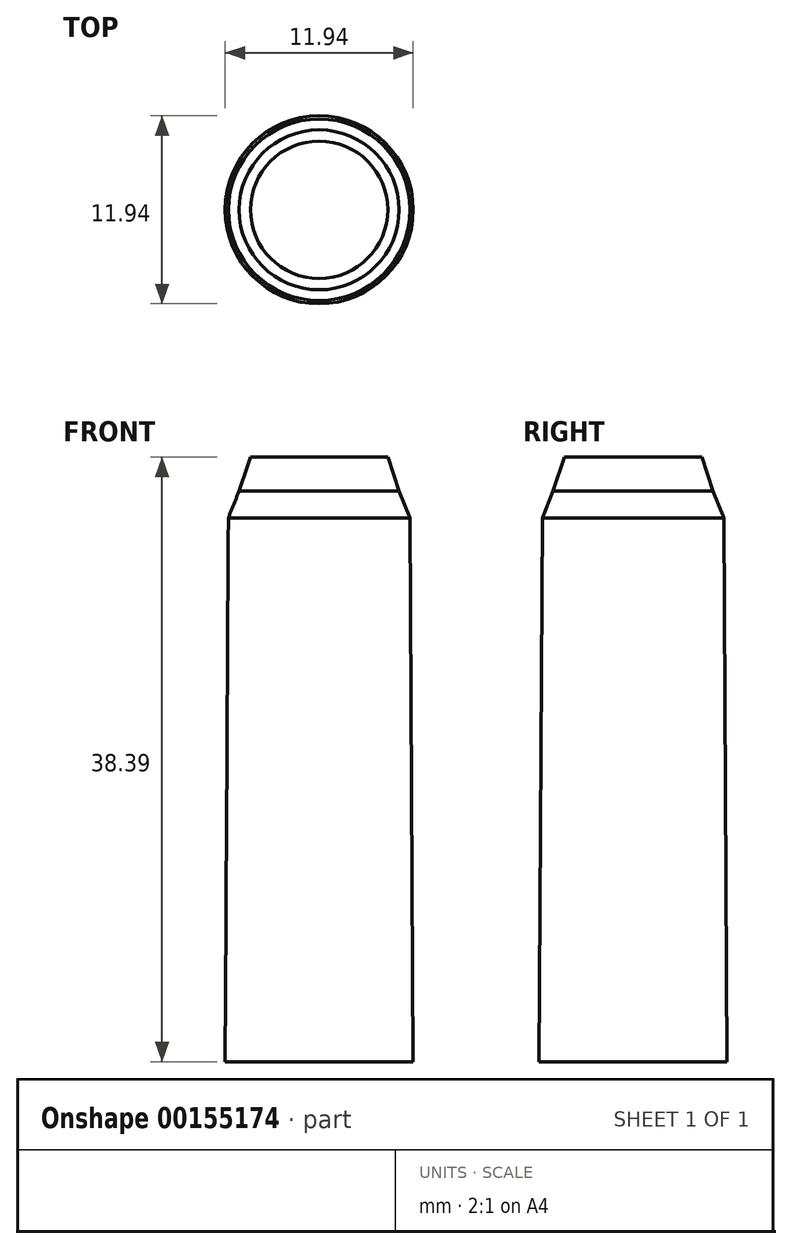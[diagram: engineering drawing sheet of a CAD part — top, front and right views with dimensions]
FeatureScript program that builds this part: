
annotation { "Feature Type Name" : "Feature", "Feature Type Description" : "" }
export const myFeature = defineFeature(function(context is Context, id is Id, definition is map)
    precondition{}
    {
        {
            var Q0;
            Q0=qCreatedBy(makeId("Front.planeOp"),FACE);
            var sketch = newSketch(context, id + "F0", { "sketchPlane" : qUnion([Q0])});
            skLineSegment(sketch, "E0", {"start": v(0, 0) * mm, "end": v(0, 38.4) * mm});
            skLineSegment(sketch, "E1", {"start": v(0, 0) * mm, "end": v(5.97, 0) * mm});
            skLineSegment(sketch, "E2", {"start": v(0, 38.4) * mm, "end": v(4.36, 38.4) * mm});
            skLineSegment(sketch, "E3", {"start": v(5.08, 36.25) * mm, "end": v(4.36, 38.4) * mm});
            skLineSegment(sketch, "E4", {"start": v(5.77, 34.54) * mm, "end": v(5.08, 36.25) * mm});
            skLineSegment(sketch, "E5", {"start": v(5.77, 34.54) * mm, "end": v(5.97, 0) * mm});
            skSolve(sketch);
        }
        {
            var Q0;
            Q0 = qSketchRegion(id + "F0", true);
            var Q1;
            Q1=sQuery(id+"F0.wireOp",EDGE,"E0");
            revolve(context, id + "F1", {"entities" : qUnion([Q0]), "axis" : qUnion([Q1]), "revolveType" : RevolveType.FULL});
        }
    });
